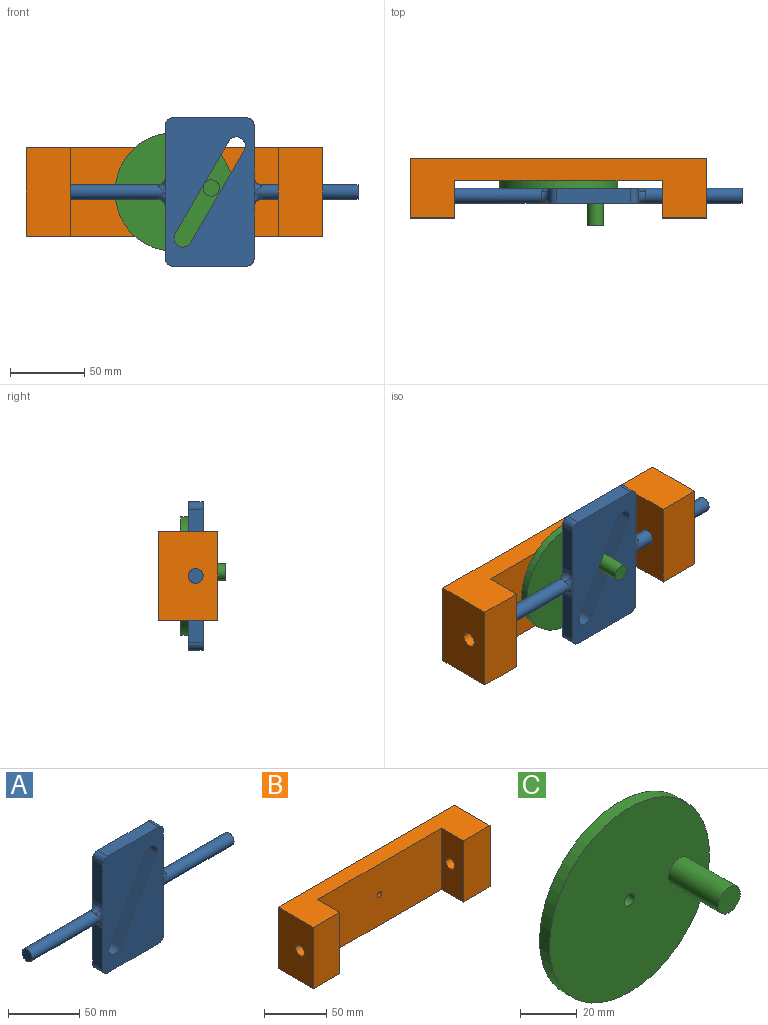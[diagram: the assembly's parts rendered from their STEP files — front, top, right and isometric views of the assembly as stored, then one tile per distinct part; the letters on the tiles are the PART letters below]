
ASSEMBLY  parts=3 mates=3
PART A: 32 faces, bbox 200x14.7x100 mm
  f0: plane 36.34x10mm, normal (-1,0,0), area 354.3mm2, adj f6,f7,f17,f29
  f1: plane 36.34x10mm, normal (1,0,0), area 354.3mm2, adj f6,f7,f26,f31
  f2: plane 50x10mm, normal (0,0,1), area 500mm2, adj f6,f7,f28,f31
  f3: plane 36.34x10mm, normal (-1,0,0), area 354.3mm2, adj f6,f7,f23,f28
  f4: plane 50x10mm, normal (0,0,-1), area 500mm2, adj f6,f7,f29,f30
  f5: plane 36.34x10mm, normal (1,0,0), area 354.3mm2, adj f6,f7,f20,f30
  f6: plane 100x60mm, normal (0,-1,0), area 5001.4mm2, adj f0,f1,f2,f3,f4,f5,f8,f9
  f7: plane 100x60mm, normal (0,1,0), area 5001.4mm2, adj f0,f1,f2,f3,f4,f5,f8,f9
  f8: plane 62.35x36mm, normal (-0.87,0,0.5), area 720mm2, adj f6,f7,f9,f11
  f9: cylinder r=6mm len=11.2mm, axis (0,-1,0), area 188.5mm2, adj f6,f7,f8,f10
  f10: plane 62.35x36mm, normal (0.87,0,-0.5), area 720mm2, adj f6,f7,f9,f11
  f11: cylinder r=6mm len=11.2mm, axis (0,-1,0), area 188.5mm2, adj f6,f7,f8,f10
  f12: cylinder r=5mm len=70mm, axis (-1,0,0), area 2081.7mm2, adj f13,f19,f20,f21,f25,f26,f27
  f13: plane 10x10mm, normal (1,0,0), area 78.5mm2, adj f12
  f14: cylinder r=5mm len=70mm, axis (1,0,0), area 2081.7mm2, adj f15,f16,f17,f18,f22,f23,f24
  f15: plane 10x10mm, normal (-1,0,0), area 78.5mm2, adj f14
  f16: bspline ~8.96x5.25mm, area 22.2mm2, adj f6,f14,f17
  f17: torus R=10mm, axis (1,0,0), area 56.1mm2, adj f0,f14,f16,f18
  f18: bspline ~8.96x5.25mm, area 22.2mm2, adj f7,f14,f17
  f19: bspline ~8.96x5.25mm, area 22.2mm2, adj f7,f12,f20
  f20: torus R=10mm, axis (1,0,0), area 56.1mm2, adj f5,f12,f19,f21
  f21: bspline ~8.96x5.25mm, area 22.2mm2, adj f6,f12,f20
  f22: bspline ~8.96x5.25mm, area 22.2mm2, adj f7,f14,f23
  f23: torus R=10mm, axis (1,0,0), area 56.1mm2, adj f3,f14,f22,f24
  f24: bspline ~8.96x5.25mm, area 22.2mm2, adj f6,f14,f23
  f25: bspline ~8.96x5.25mm, area 22.2mm2, adj f6,f12,f26
  f26: torus R=10mm, axis (1,0,0), area 56.1mm2, adj f1,f12,f25,f27
  f27: bspline ~8.96x5.25mm, area 22.2mm2, adj f7,f12,f26
  f28: cylinder r=5mm len=10mm, axis (0,-1,0), area 78.5mm2, adj f2,f3,f6,f7
  f29: cylinder r=5mm len=10mm, axis (0,1,0), area 78.5mm2, adj f0,f4,f6,f7
  f30: cylinder r=5mm len=10mm, axis (0,-1,0), area 78.5mm2, adj f4,f5,f6,f7
  f31: cylinder r=5mm len=10mm, axis (0,1,0), area 78.5mm2, adj f1,f2,f6,f7
PART B: 13 faces, bbox 200x40x60 mm
  f0: plane 140x60mm, normal (0,-1,0), area 8380.4mm2, adj f1,f3,f6,f7,f9
  f1: plane 200x40mm, normal (0,0,1), area 4500mm2, adj f0,f2,f4,f5,f7,f8,f9,f10
  f2: plane 60x40mm, normal (-1,0,0), area 2321.5mm2, adj f1,f3,f5,f8,f12
  f3: plane 200x40mm, normal (0,0,-1), area 4500mm2, adj f0,f2,f4,f5,f7,f8,f9,f10
  f4: plane 60x40mm, normal (1,0,0), area 2321.5mm2, adj f1,f3,f5,f10,f11
  f5: plane 200x60mm, normal (0,1,0), area 11980.4mm2, adj f1,f2,f3,f4,f6
  f6: cylinder r=2.5mm len=15mm, axis (0,-1,0), area 235.6mm2, adj f0,f5
  f7: plane 60x25mm, normal (1,0,0), area 1421.5mm2, adj f0,f1,f3,f8,f12
  f8: plane 60x30mm, normal (0,-1,0), area 1800mm2, adj f1,f2,f3,f7
  f9: plane 60x25mm, normal (-1,0,0), area 1421.5mm2, adj f0,f1,f3,f10,f11
  f10: plane 60x30mm, normal (0,-1,0), area 1800mm2, adj f1,f3,f4,f9
  f11: cylinder r=5mm len=30mm, axis (1,0,0), area 942.5mm2, adj f4,f9
  f12: cylinder r=5mm len=30mm, axis (1,0,0), area 942.5mm2, adj f2,f7
PART C: 6 faces, bbox 80x30x80 mm
  f0: cylinder r=40mm len=80mm, axis (0,1,0), area 1256.6mm2, adj f1,f2
  f1: plane 80x80mm, normal (0,-1,0), area 4911.9mm2, adj f0,f3,f4
  f2: plane 80x80mm, normal (0,1,0), area 5006.9mm2, adj f0,f3
  f3: cylinder r=2.5mm len=5mm, axis (0,-1,0), area 78.5mm2, adj f1,f2
  f4: cylinder r=5.5mm len=25mm, axis (0,1,0), area 863.9mm2, adj f1,f5
  f5: plane 11x11mm, normal (0,-1,0), area 95mm2, adj f4
PLACE A t=(23.84,-25,0)mm
PLACE B at identity fixed
PLACE C rot(axis=(0,-1,0),6.3deg) t=(0,-17.5,0)mm
MATE slider A.f17 <-> B.f11  axis (-1,0,0) through (-76.16,-25,0)mm
MATE planar A.f7 <-> C.f1  axis (0,1,0) through (23.84,-20,50)mm
MATE revolute C.f3 <-> B.f6  axis (0,1,0) through (0,-15,0)mm
